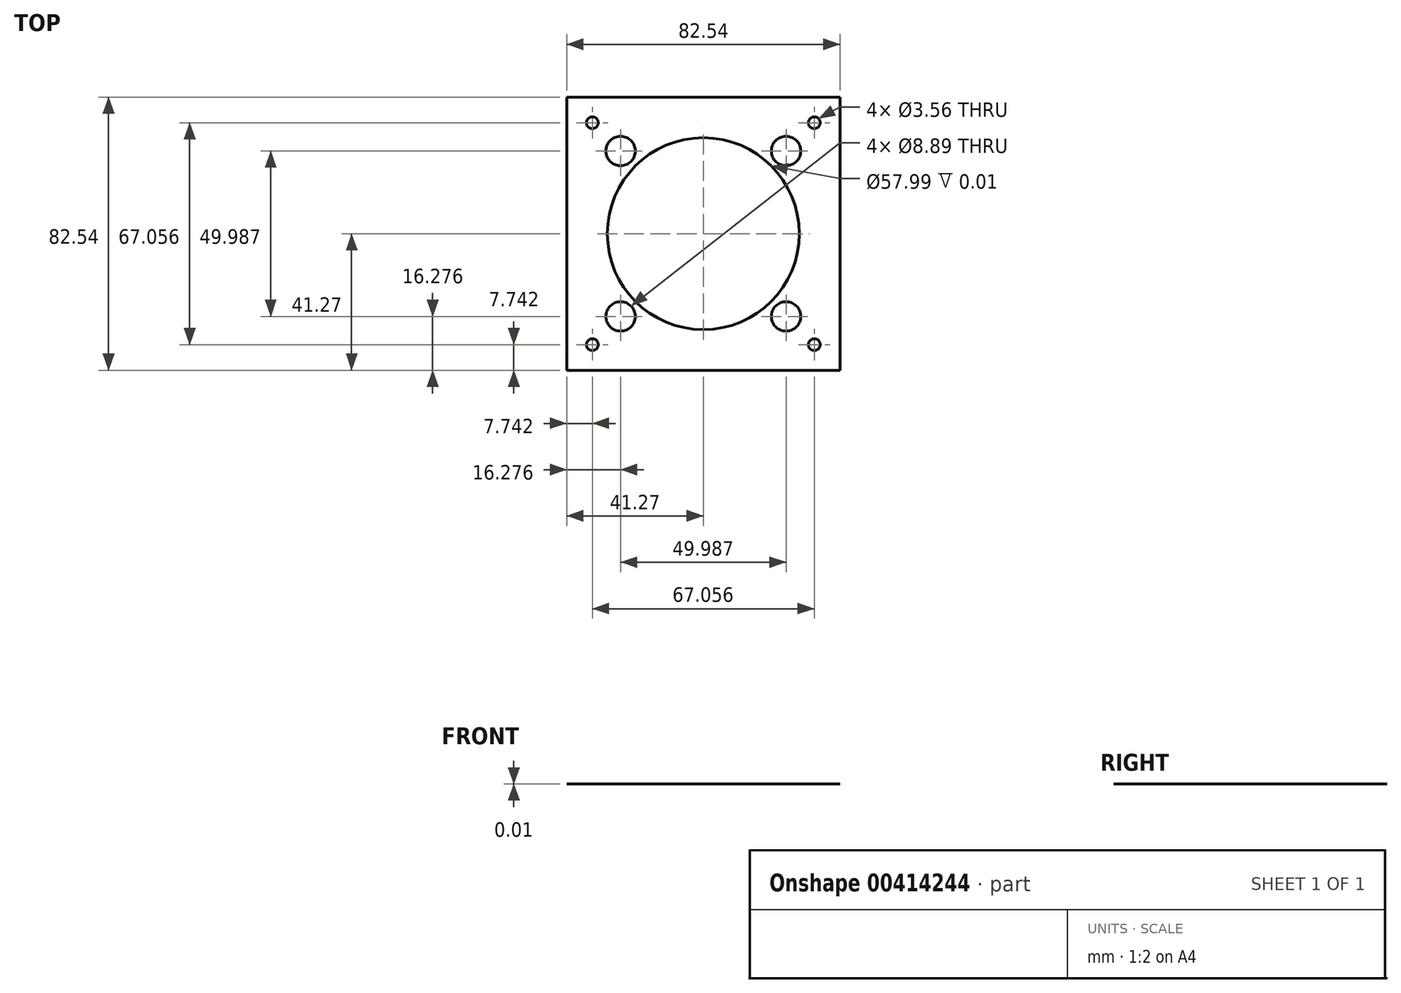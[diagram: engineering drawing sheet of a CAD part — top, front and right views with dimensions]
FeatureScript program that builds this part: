
annotation { "Feature Type Name" : "Feature", "Feature Type Description" : "" }
export const myFeature = defineFeature(function(context is Context, id is Id, definition is map)
    precondition{}
    {
        {
            var Q0;
            Q0=qCreatedBy(makeId("Top.planeOp"),FACE);
            var sketch = newSketch(context, id + "F0", { "sketchPlane" : qUnion([Q0])});
            skLineSegment(sketch, "E0.bottom", {"start": v(41.28, 41.28) * mm, "end": v(-41.28, 41.28) * mm});
            skLineSegment(sketch, "E0.top", {"start": v(41.28, -41.28) * mm, "end": v(-41.28, -41.28) * mm});
            skLineSegment(sketch, "E0.left", {"start": v(41.28, 41.28) * mm, "end": v(41.28, -41.28) * mm});
            skLineSegment(sketch, "E0.right", {"start": v(-41.28, 41.28) * mm, "end": v(-41.28, -41.28) * mm});
            skCircle(sketch, "E1", {"center": v(0, 0) * mm, "radius": 29 * mm});
            skLineSegment(sketch, "E2", {"start": v(0, 0) * mm, "end": v(0, 25) * mm, "construction": true});
            skLineSegment(sketch, "E3", {"start": v(0, 25) * mm, "end": v(25, 25) * mm, "construction": true});
            skCircle(sketch, "E4", {"center": v(25, 25) * mm, "radius": 4.45 * mm});
            skCircle(sketch, "E5.1.0", {"center": v(-25, 25) * mm, "radius": 4.45 * mm});
            skCircle(sketch, "E5.2.0", {"center": v(-25, -25) * mm, "radius": 4.45 * mm});
            skCircle(sketch, "E5.3.0", {"center": v(25, -25) * mm, "radius": 4.45 * mm});
            skLineSegment(sketch, "E6", {"start": v(0, 0) * mm, "end": v(41.28, 41.28) * mm, "construction": true});
            skCircle(sketch, "E7", {"center": v(33.53, 33.53) * mm, "radius": 1.78 * mm});
            skCircle(sketch, "E8.1.0", {"center": v(-33.53, 33.53) * mm, "radius": 1.78 * mm});
            skCircle(sketch, "E8.2.0", {"center": v(-33.53, -33.53) * mm, "radius": 1.78 * mm});
            skCircle(sketch, "E8.3.0", {"center": v(33.53, -33.53) * mm, "radius": 1.78 * mm});
            skLineSegment(sketch, "E9", {"start": v(0, 0) * mm, "end": v(41.28, 0) * mm, "construction": true});
            skSolve(sketch);
        }
        {
            var Q0;
            Q0=makeQuery(id+"F0.imprint","IMPRINT",FACE,{"disambiguationData":[TD([[makeQuery(id+"F0.imprint","IMPRINT",EDGE,{"derivedFrom":sQuery(id+"F0.wireOp",EDGE,"E0.bottom")}),1.0]])]});
            extrude(context, id + "F1", {"entities" : qUnion([Q0]), "depth" : 1 / 101.6 * mm});
        }
    });
